FCSTD DOCUMENT  (FreeCAD 0.19R24267 (Git))
Label: MasterSketch
License: All rights reserved
LicenseURL: http://en.wikipedia.org/wiki/All_rights_reserved
objects: PartDesign::CoordinateSystem×3, Sketcher::SketchObject×1, PartDesign::Body×1, App::Part×1
note: 5 computed .brp shape members not serialized (recipe doc carries the construction recipe); baked Part::Feature solids carry a one-line shape summary decoded from their .brp

FEATURE [Sketcher::SketchObject] Sketch
  FullyConstrained = true
  MapMode = 5
  Support = -> [XY_Plane001]
  expr: Constraints[16] = 35 / 2
  sketch-geometry (7):
    g0: LineSegment StartX=-100 StartY=37.5 StartZ=0 EndX=100 EndY=37.5 EndZ=0
    g1: LineSegment StartX=100 StartY=37.5 StartZ=0 EndX=100 EndY=-37.5 EndZ=0
    g2: LineSegment StartX=100 StartY=-37.5 StartZ=0 EndX=-100 EndY=-37.5 EndZ=0
    g3: LineSegment StartX=-100 StartY=-37.5 StartZ=0 EndX=-100 EndY=37.5 EndZ=0
    g4: Circle CenterX=0 CenterY=0 CenterZ=0 NormalX=0 NormalY=0 NormalZ=1 AngleXU=0 Radius=17.5
    g5: Circle CenterX=-50 CenterY=0 CenterZ=0 NormalX=0 NormalY=0 NormalZ=1 AngleXU=0 Radius=17.5
    g6: Circle CenterX=50 CenterY=0 CenterZ=0 NormalX=0 NormalY=0 NormalZ=1 AngleXU=0 Radius=17.5
  constraints (18):
    c: Coincident(g0,g1)
    c: Coincident(g1,g2)
    c: Coincident(g2,g3)
    c: Coincident(g3,g0)
    c: Horizontal(g0)
    c: Horizontal(g2)
    c: Vertical(g1)
    c: Vertical(g3)
    c: Symmetric(g0,g1,g-1)
    c: DistanceX(g0,g0) = 200
    c: DistanceY(g3,g3) = 75
    c: Coincident(g4,g-1)
    c: PointOnObject(g5,g-1)
    c: Equal(g5,g4)
    c: Equal(g4,g6)
    c: Symmetric(g5,g6,g-2)
    c: Radius(g5) = 17.5
    c: DistanceX(g5,g4) = 50
FEATURE [PartDesign::CoordinateSystem] CircleLeft
  AttacherType = Attacher::AttachEngine3D
  AttachmentOffset = pos=(0,0,0) rot=(0,0,1;1.5708rad)
  MapMode = 11
  Placement = pos=(-50,0,0) rot=(0,0,1;3.14159rad)
  Support = -> [Sketch]
FEATURE [PartDesign::CoordinateSystem] CircleCenter
  AttacherType = Attacher::AttachEngine3D
  AttachmentOffset = pos=(0,0,0) rot=(0,0,1;1.5708rad)
  MapMode = 11
  Placement = pos=(0,0,0) rot=(0,0,1;3.14159rad)
  Support = -> [Sketch]
FEATURE [PartDesign::CoordinateSystem] CircleRight
  AttacherType = Attacher::AttachEngine3D
  AttachmentOffset = pos=(0,0,0) rot=(0,0,1;1.5708rad)
  MapMode = 11
  Placement = pos=(50,0,0) rot=(0,0,1;3.14159rad)
  Support = -> [Sketch]
FEATURE [PartDesign::Body] Body  label="MasterSketchBody"
  Group = -> [Sketch,CircleLeft,CircleCenter,CircleRight]
  Origin = -> Origin001
FEATURE [App::Part] Part
  Group = -> [Body]
  Origin = -> Origin
